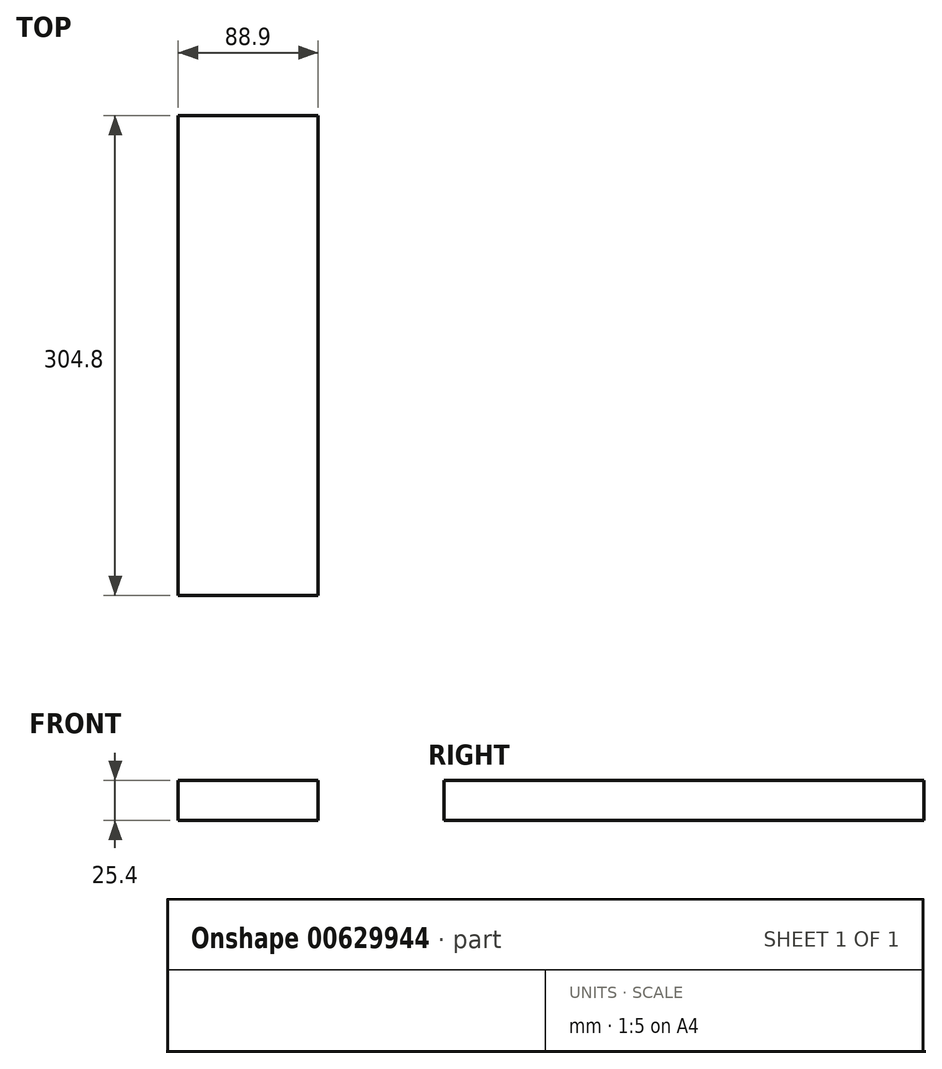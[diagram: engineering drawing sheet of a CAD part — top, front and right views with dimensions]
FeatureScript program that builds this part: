
annotation { "Feature Type Name" : "Feature", "Feature Type Description" : "" }
export const myFeature = defineFeature(function(context is Context, id is Id, definition is map)
    precondition{}
    {
        {
            var Q0;
            Q0=qCreatedBy(makeId("Front.planeOp"),FACE);
            var sketch = newSketch(context, id + "F0", { "sketchPlane" : qUnion([Q0])});
            skLineSegment(sketch, "E0.bottom", {"start": v(-37.9, 25.4) * mm, "end": v(51, 25.4) * mm});
            skLineSegment(sketch, "E0.top", {"start": v(-37.9, 0) * mm, "end": v(51, 0) * mm});
            skLineSegment(sketch, "E0.left", {"start": v(-37.9, 25.4) * mm, "end": v(-37.9, 0) * mm});
            skLineSegment(sketch, "E0.right", {"start": v(51, 25.4) * mm, "end": v(51, 0) * mm});
            skSolve(sketch);
        }
        {
            var Q0;
            Q0 = qSketchRegion(id + "F0", true);
            extrude(context, id + "F1", {"entities" : qUnion([Q0]), "depth" : 304.8 * mm, "offsetDistance" : 25.4 * mm});
        }
    });
